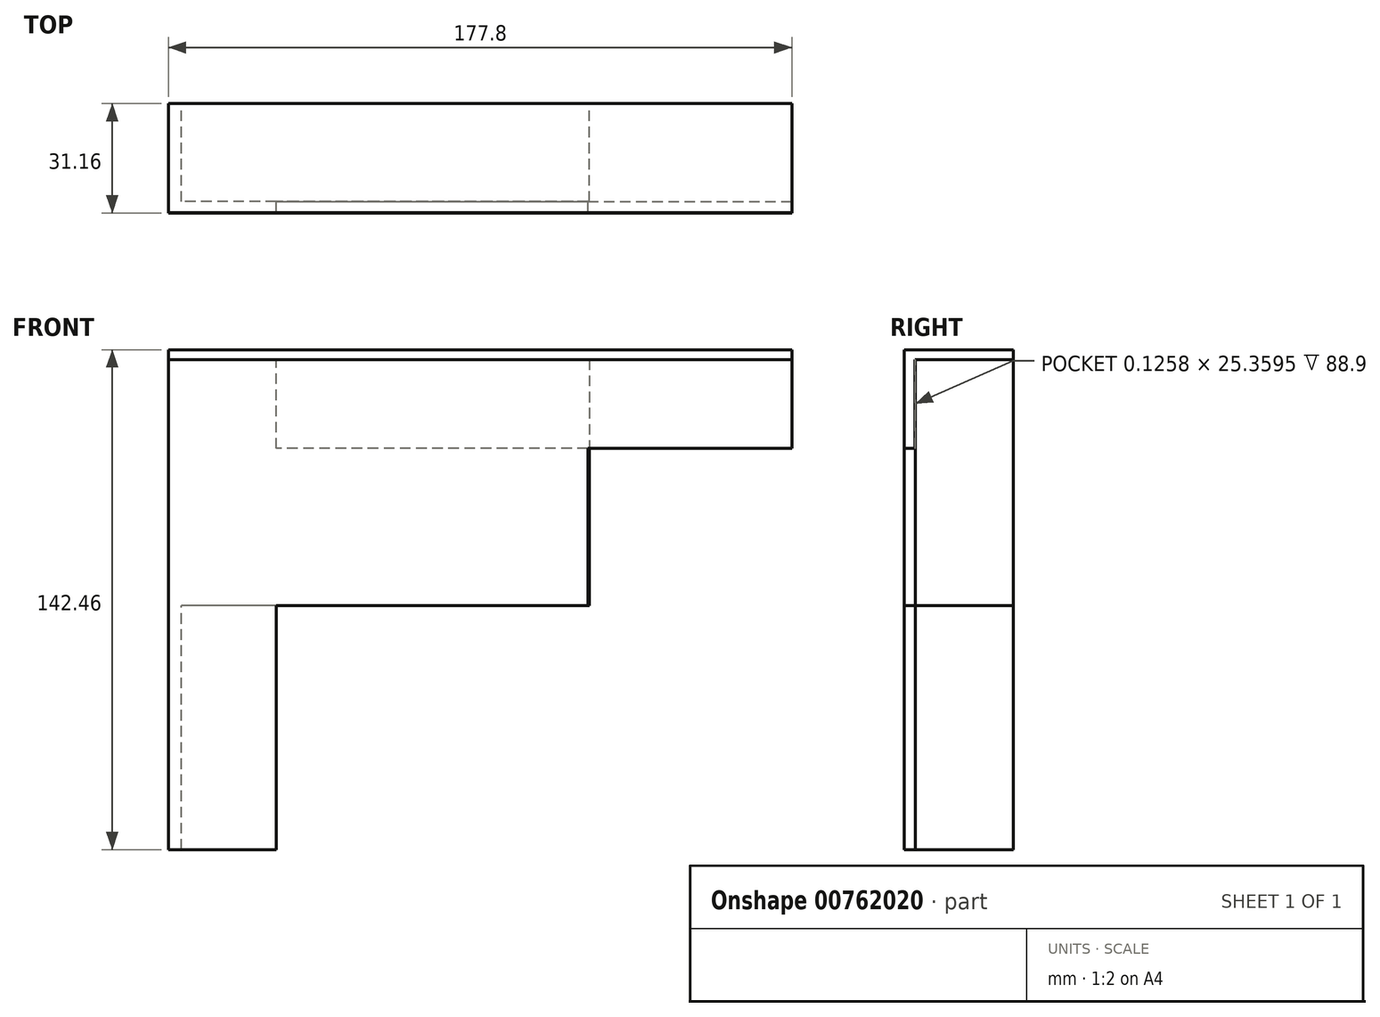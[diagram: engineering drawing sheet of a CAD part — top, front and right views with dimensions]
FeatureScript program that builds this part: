
annotation { "Feature Type Name" : "Feature", "Feature Type Description" : "" }
export const myFeature = defineFeature(function(context is Context, id is Id, definition is map)
    precondition{}
    {
        {
            var Q0;
            Q0=qCreatedBy(makeId("Front.planeOp"),FACE);
            var sketch = newSketch(context, id + "F0", { "sketchPlane" : qUnion([Q0])});
            skLineSegment(sketch, "E0.bottom", {"start": v(58.13, 35.08) * mm, "end": v(-58.13, 35.08) * mm});
            skLineSegment(sketch, "E0.top", {"start": v(58.13, -35.08) * mm, "end": v(-58.13, -35.08) * mm});
            skLineSegment(sketch, "E0.left", {"start": v(58.13, 35.08) * mm, "end": v(58.13, -35.08) * mm});
            skLineSegment(sketch, "E0.right", {"start": v(-58.13, 35.08) * mm, "end": v(-58.13, -35.08) * mm});
            skPoint(sketch, "E0.middle", {"position": v(0, 0) * mm});
            skSolve(sketch);
        }
        {
            var Q0;
            Q0=makeQuery(id+"F0.imprint","IMPRINT",FACE,{"disambiguationData":[TD([[makeQuery(id+"F0.imprint","IMPRINT",EDGE,{"derivedFrom":sQuery(id+"F0.wireOp",EDGE,"E0.bottom")}),1.0]])]});
            extrude(context, id + "F1", {"entities" : qUnion([Q0]), "depth" : 27.94 * mm, "offsetDistance" : 25.4 * mm});
        }
        {
            var Q0;
            Q0=makeQuery(id+"F1.opExtrude","SWEPT_FACE",FACE,{"disambiguationData":[OSD([sQuery(id+"F0.wireOp",EDGE,"E0.bottom")])]});
            var sketch = newSketch(context, id + "F2", { "sketchPlane" : qUnion([Q0])});
            skLineSegment(sketch, "E1.bottom", {"start": v(-58.13, -27.94) * mm, "end": v(-61.92, -27.94) * mm});
            skLineSegment(sketch, "E1.top", {"start": v(-58.13, 0) * mm, "end": v(-61.92, 0) * mm});
            skLineSegment(sketch, "E1.left", {"start": v(-58.13, -27.94) * mm, "end": v(-58.13, 0) * mm});
            skLineSegment(sketch, "E1.right", {"start": v(-61.92, -27.94) * mm, "end": v(-61.92, 0) * mm});
            skLineSegment(sketch, "E2.bottom", {"start": v(-61.92, -27.94) * mm, "end": v(-31.15, -27.94) * mm});
            skLineSegment(sketch, "E2.top", {"start": v(-61.92, -31.16) * mm, "end": v(-31.15, -31.16) * mm});
            skLineSegment(sketch, "E2.left", {"start": v(-61.92, -27.94) * mm, "end": v(-61.92, -31.16) * mm});
            skLineSegment(sketch, "E2.right", {"start": v(-31.15, -27.94) * mm, "end": v(-31.15, -31.16) * mm});
            skSolve(sketch);
        }
        {
            var Q0;
            Q0=makeQuery(id+"F2.imprint","IMPRINT",FACE,{"disambiguationData":[TD([[makeQuery(id+"F2.imprint","IMPRINT",EDGE,{"derivedFrom":sQuery(id+"F2.wireOp",EDGE,"E1.top")}),1.0]])]});
            var Q1;
            Q1=makeQuery(id+"F2.imprint","IMPRINT",FACE,{"disambiguationData":[TD([[makeQuery(id+"F2.imprint","IMPRINT",EDGE,{"derivedFrom":sQuery(id+"F2.wireOp",EDGE,"E2.top")}),1.0]])]});
            extrude(context, id + "F3", {"entities" : qUnion([Q0, Q1]), "operationType" : NewBodyOperationType.ADD, "oppositeDirection" : true, "depth" : 139.7 * mm, "offsetDistance" : 25.4 * mm});
        }
        {
            var Q0;
            Q0=makeQuery(id+"F3.opExtrude","SWEPT_FACE",FACE,{"disambiguationData":[OSD([sQuery(id+"F2.wireOp",EDGE,"E1.right"),sQuery(id+"F2.wireOp",EDGE,"E2.left")])]});
            var sketch = newSketch(context, id + "F4", { "sketchPlane" : qUnion([Q0])});
            skLineSegment(sketch, "E3.bottom", {"start": v(0, 35.08) * mm, "end": v(31.07, 35.08) * mm});
            skLineSegment(sketch, "E3.top", {"start": v(0, 37.84) * mm, "end": v(31.07, 37.84) * mm});
            skLineSegment(sketch, "E3.left", {"start": v(0, 35.08) * mm, "end": v(0, 37.84) * mm});
            skLineSegment(sketch, "E3.right", {"start": v(31.07, 35.08) * mm, "end": v(31.07, 37.84) * mm});
            skLineSegment(sketch, "E4.bottom", {"start": v(28.07, 37.84) * mm, "end": v(31.16, 37.84) * mm});
            skLineSegment(sketch, "E4.top", {"start": v(28.07, 9.72) * mm, "end": v(31.16, 9.72) * mm});
            skLineSegment(sketch, "E4.left", {"start": v(28.07, 37.84) * mm, "end": v(28.07, 9.72) * mm});
            skLineSegment(sketch, "E4.right", {"start": v(31.16, 37.84) * mm, "end": v(31.16, 9.72) * mm});
            skSolve(sketch);
        }
        {
            var Q0;
            {var subQ4=sQuery(id+"F4.wireOp",EDGE,"E3.top");Q0=makeQuery(id+"F4.imprint","IMPRINT",FACE,{"disambiguationData":[TD([[makeQuery(id+"F4.imprint","IMPRINT",EDGE,{"derivedFrom":subQ4}),-1.0]])]});}
            var Q1;
            {var subQ4=sQuery(id+"F4.wireOp",EDGE,"E4.top");Q1=makeQuery(id+"F4.imprint","IMPRINT",FACE,{"disambiguationData":[TD([[makeQuery(id+"F4.imprint","IMPRINT",EDGE,{"derivedFrom":subQ4}),1.0]])]});}
            var Q2;
            {var subQ0=sQuery(id+"F4.wireOp",EDGE,"E3.right");Q2=makeQuery(id+"F4.imprint","IMPRINT",FACE,{"disambiguationData":[TD([[makeQuery(id+"F4.imprint","IMPRINT",EDGE,{"derivedFrom":subQ0}),1.0]])]});}
            extrude(context, id + "F5", {"entities" : qUnion([Q0, Q1, Q2]), "operationType" : NewBodyOperationType.ADD, "oppositeDirection" : true, "depth" : 177.8 * mm, "offsetDistance" : 25.4 * mm});
        }
        {
            var Q0;
            Q0=makeQuery(id+"F3.opExtrude","SWEPT_FACE",FACE,{"disambiguationData":[OSD([sQuery(id+"F2.wireOp",EDGE,"E2.right")])]});
            var sketch = newSketch(context, id + "F6", { "sketchPlane" : qUnion([Q0])});
            skLineSegment(sketch, "E5.bottom", {"start": v(-31.16, 9.72) * mm, "end": v(-27.94, 9.72) * mm});
            skLineSegment(sketch, "E5.top", {"start": v(-31.16, -35.08) * mm, "end": v(-27.94, -35.08) * mm});
            skLineSegment(sketch, "E5.left", {"start": v(-31.16, 9.72) * mm, "end": v(-31.16, -35.08) * mm});
            skLineSegment(sketch, "E5.right", {"start": v(-27.94, 9.72) * mm, "end": v(-27.94, -35.08) * mm});
            skSolve(sketch);
        }
        {
            var Q0;
            Q0=makeQuery(id+"F6.imprint","IMPRINT",FACE,{"disambiguationData":[TD([[makeQuery(id+"F6.imprint","IMPRINT",EDGE,{"derivedFrom":sQuery(id+"F6.wireOp",EDGE,"E5.top")}),1.0]])]});
            extrude(context, id + "F7", {"entities" : qUnion([Q0]), "operationType" : NewBodyOperationType.ADD, "depth" : 88.9 * mm, "offsetDistance" : 25.4 * mm});
        }
    });
